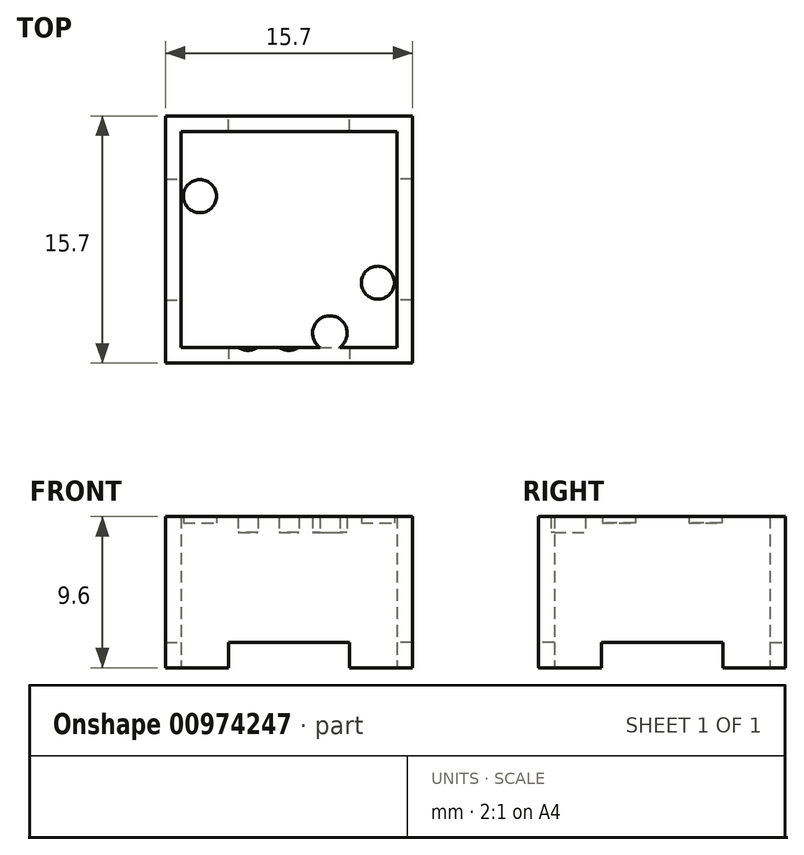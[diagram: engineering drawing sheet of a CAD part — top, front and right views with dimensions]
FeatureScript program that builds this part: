
annotation { "Feature Type Name" : "Feature", "Feature Type Description" : "" }
export const myFeature = defineFeature(function(context is Context, id is Id, definition is map)
    precondition{}
    {
        {
            var Q0;
            Q0=qCreatedBy(makeId("Top.planeOp"),FACE);
            var sketch = newSketch(context, id + "F0", { "sketchPlane" : qUnion([Q0])});
            skLineSegment(sketch, "E0.bottom", {"start": v(-7.85, 7.85) * mm, "end": v(7.85, 7.85) * mm});
            skLineSegment(sketch, "E0.top", {"start": v(-7.85, -7.85) * mm, "end": v(7.85, -7.85) * mm});
            skLineSegment(sketch, "E0.left", {"start": v(-7.85, 7.85) * mm, "end": v(-7.85, -7.85) * mm});
            skLineSegment(sketch, "E0.right", {"start": v(7.85, 7.85) * mm, "end": v(7.85, -7.85) * mm});
            skLineSegment(sketch, "E1", {"start": v(7.85, 7.85) * mm, "end": v(-7.85, -7.85) * mm, "construction": true});
            skLineSegment(sketch, "E2", {"start": v(-7.85, 3.85) * mm, "end": v(-6.85, 3.85) * mm});
            skLineSegment(sketch, "E3", {"start": v(-6.85, 3.85) * mm, "end": v(-6.85, 6.85) * mm});
            skLineSegment(sketch, "E4", {"start": v(-6.85, 6.85) * mm, "end": v(-3.85, 6.85) * mm});
            skLineSegment(sketch, "E5", {"start": v(-3.85, 6.85) * mm, "end": v(-3.85, 7.85) * mm});
            skLineSegment(sketch, "E6.MirrorCS", {"start": v(7.85, 3.85) * mm, "end": v(6.85, 3.85) * mm});
            skLineSegment(sketch, "E7.MirrorCS", {"start": v(6.85, 3.85) * mm, "end": v(6.85, 6.85) * mm});
            skLineSegment(sketch, "E8.MirrorCS", {"start": v(3.85, 6.85) * mm, "end": v(3.85, 7.85) * mm});
            skLineSegment(sketch, "E9.MirrorCS", {"start": v(6.85, 6.85) * mm, "end": v(3.85, 6.85) * mm});
            skLineSegment(sketch, "E10.MirrorCS", {"start": v(-7.85, -3.85) * mm, "end": v(-6.85, -3.85) * mm});
            skLineSegment(sketch, "E11.MirrorCS", {"start": v(-6.85, -3.85) * mm, "end": v(-6.85, -6.85) * mm});
            skLineSegment(sketch, "E12.MirrorCS", {"start": v(-6.85, -6.85) * mm, "end": v(-3.85, -6.85) * mm});
            skLineSegment(sketch, "E13.MirrorCS", {"start": v(-3.85, -6.85) * mm, "end": v(-3.85, -7.85) * mm});
            skLineSegment(sketch, "E14.MirrorCS", {"start": v(3.85, -6.85) * mm, "end": v(3.85, -7.85) * mm});
            skLineSegment(sketch, "E15.MirrorCS", {"start": v(6.85, -6.85) * mm, "end": v(3.85, -6.85) * mm});
            skLineSegment(sketch, "E16.MirrorCS", {"start": v(6.85, -3.85) * mm, "end": v(6.85, -6.85) * mm});
            skLineSegment(sketch, "E17.MirrorCS", {"start": v(7.85, -3.85) * mm, "end": v(6.85, -3.85) * mm});
            skLineSegment(sketch, "E18", {"start": v(-3.85, 6.85) * mm, "end": v(3.85, 6.85) * mm});
            skLineSegment(sketch, "E19", {"start": v(6.85, 3.85) * mm, "end": v(6.85, -3.85) * mm});
            skLineSegment(sketch, "E20", {"start": v(3.85, -6.85) * mm, "end": v(-3.85, -6.85) * mm});
            skLineSegment(sketch, "E21", {"start": v(-6.85, -3.85) * mm, "end": v(-6.85, 3.85) * mm});
            skSolve(sketch);
        }
        {
            var Q0;
            Q0 = qSketchRegion(id + "F0", true);
            extrude(context, id + "F1", {"entities" : qUnion([Q0]), "depth" : 9.6 * mm, "offsetDistance" : 25 * mm});
        }
        {
            var Q0;
            {var subQ0=sQuery(id+"F0.wireOp",EDGE,"E5");Q0=makeQuery(id+"F0.imprint","IMPRINT",FACE,{"disambiguationData":[TD([[makeQuery(id+"F0.imprint","IMPRINT",EDGE,{"derivedFrom":subQ0}),-1.0]])]});}
            var Q1;
            {var subQ0=sQuery(id+"F0.wireOp",EDGE,"E6.MirrorCS");Q1=makeQuery(id+"F0.imprint","IMPRINT",FACE,{"disambiguationData":[TD([[makeQuery(id+"F0.imprint","IMPRINT",EDGE,{"derivedFrom":subQ0}),1.0]])]});}
            var Q2;
            {var subQ0=sQuery(id+"F0.wireOp",EDGE,"E13.MirrorCS");Q2=makeQuery(id+"F0.imprint","IMPRINT",FACE,{"disambiguationData":[TD([[makeQuery(id+"F0.imprint","IMPRINT",EDGE,{"derivedFrom":subQ0}),1.0]])]});}
            var Q3;
            {var subQ0=sQuery(id+"F0.wireOp",EDGE,"E2");Q3=makeQuery(id+"F0.imprint","IMPRINT",FACE,{"disambiguationData":[TD([[makeQuery(id+"F0.imprint","IMPRINT",EDGE,{"derivedFrom":subQ0}),-1.0]])]});}
            extrude(context, id + "F2", {"entities" : qUnion([Q0, Q1, Q2, Q3]), "operationType" : NewBodyOperationType.REMOVE, "depth" : 1.6 * mm, "offsetDistance" : 25 * mm});
        }
        {
            var Q0;
            Q0=makeQuery(id+"F0.imprint","IMPRINT",FACE,{"disambiguationData":[TD([[makeQuery(id+"F0.imprint","IMPRINT",EDGE,{"derivedFrom":sQuery(id+"F0.wireOp",EDGE,"E3")}),-1.0]])]});
            extrude(context, id + "F3", {"entities" : qUnion([Q0]), "operationType" : NewBodyOperationType.ADD, "depth" : 9.6 * mm, "offsetDistance" : 25 * mm, "hasSecondDirection" : true, "secondDirectionOppositeDirection" : false, "secondDirectionDepth" : 8.6 * mm});
        }
        {
            var Q0;
            Q0=makeQuery(id+"F3.opExtrude","CAP_FACE",FACE,{"disambiguationData":[OSD([sQuery(id+"F0.wireOp",EDGE,"E3"),sQuery(id+"F0.wireOp",EDGE,"E4"),sQuery(id+"F0.wireOp",EDGE,"E7.MirrorCS"),sQuery(id+"F0.wireOp",EDGE,"E9.MirrorCS"),sQuery(id+"F0.wireOp",EDGE,"E11.MirrorCS"),sQuery(id+"F0.wireOp",EDGE,"E12.MirrorCS"),sQuery(id+"F0.wireOp",EDGE,"E15.MirrorCS"),sQuery(id+"F0.wireOp",EDGE,"E16.MirrorCS"),sQuery(id+"F0.wireOp",EDGE,"E18"),sQuery(id+"F0.wireOp",EDGE,"E19"),sQuery(id+"F0.wireOp",EDGE,"E20"),sQuery(id+"F0.wireOp",EDGE,"E21")])],"isStart":true});
            var sketch = newSketch(context, id + "F4", { "sketchPlane" : qUnion([Q0])});
            skCircle(sketch, "E22", {"center": v(-2.6, 5.95) * mm, "radius": 1.1 * mm});
            skCircle(sketch, "E23", {"center": v(0, 5.95) * mm, "radius": 1.1 * mm});
            skCircle(sketch, "E24", {"center": v(-5.65, -2.75) * mm, "radius": 1.05 * mm});
            skCircle(sketch, "E25", {"center": v(5.65, 2.75) * mm, "radius": 1.05 * mm});
            skCircle(sketch, "E26.MirrorC", {"center": v(2.6, 5.95) * mm, "radius": 1.1 * mm});
            skSolve(sketch);
        }
        {
            var Q0;
            Q0=makeQuery(id+"F4.imprint","IMPRINT",FACE,{"disambiguationData":[TD([[makeQuery(id+"F4.imprint","IMPRINT",EDGE,{"derivedFrom":sQuery(id+"F4.wireOp",EDGE,"E24")}),1.0]])]});
            var Q1;
            Q1=makeQuery(id+"F4.imprint","IMPRINT",FACE,{"disambiguationData":[TD([[makeQuery(id+"F4.imprint","IMPRINT",EDGE,{"derivedFrom":sQuery(id+"F4.wireOp",EDGE,"E25")}),1.0]])]});
            extrude(context, id + "F5", {"entities" : qUnion([Q0, Q1]), "operationType" : NewBodyOperationType.REMOVE, "oppositeDirection" : true, "depth" : 0.6 * mm, "offsetDistance" : 25 * mm});
        }
        {
            var Q0;
            Q0=makeQuery(id+"F4.imprint","IMPRINT",FACE,{"disambiguationData":[TD([[makeQuery(id+"F4.imprint","IMPRINT",EDGE,{"derivedFrom":sQuery(id+"F4.wireOp",EDGE,"E22")}),1.0]])]});
            var Q1;
            Q1=makeQuery(id+"F4.imprint","IMPRINT",FACE,{"disambiguationData":[TD([[makeQuery(id+"F4.imprint","IMPRINT",EDGE,{"derivedFrom":sQuery(id+"F4.wireOp",EDGE,"E23")}),1.0]])]});
            var Q2;
            Q2=makeQuery(id+"F4.imprint","IMPRINT",FACE,{"disambiguationData":[TD([[makeQuery(id+"F4.imprint","IMPRINT",EDGE,{"derivedFrom":sQuery(id+"F4.wireOp",EDGE,"E26.MirrorC")}),-1.0]])]});
            extrude(context, id + "F6", {"entities" : qUnion([Q0, Q1, Q2]), "operationType" : NewBodyOperationType.REMOVE, "endBound" : BoundingType.THROUGH_ALL, "oppositeDirection" : true, "depth" : 25 * mm, "offsetDistance" : 25 * mm});
        }
    });
